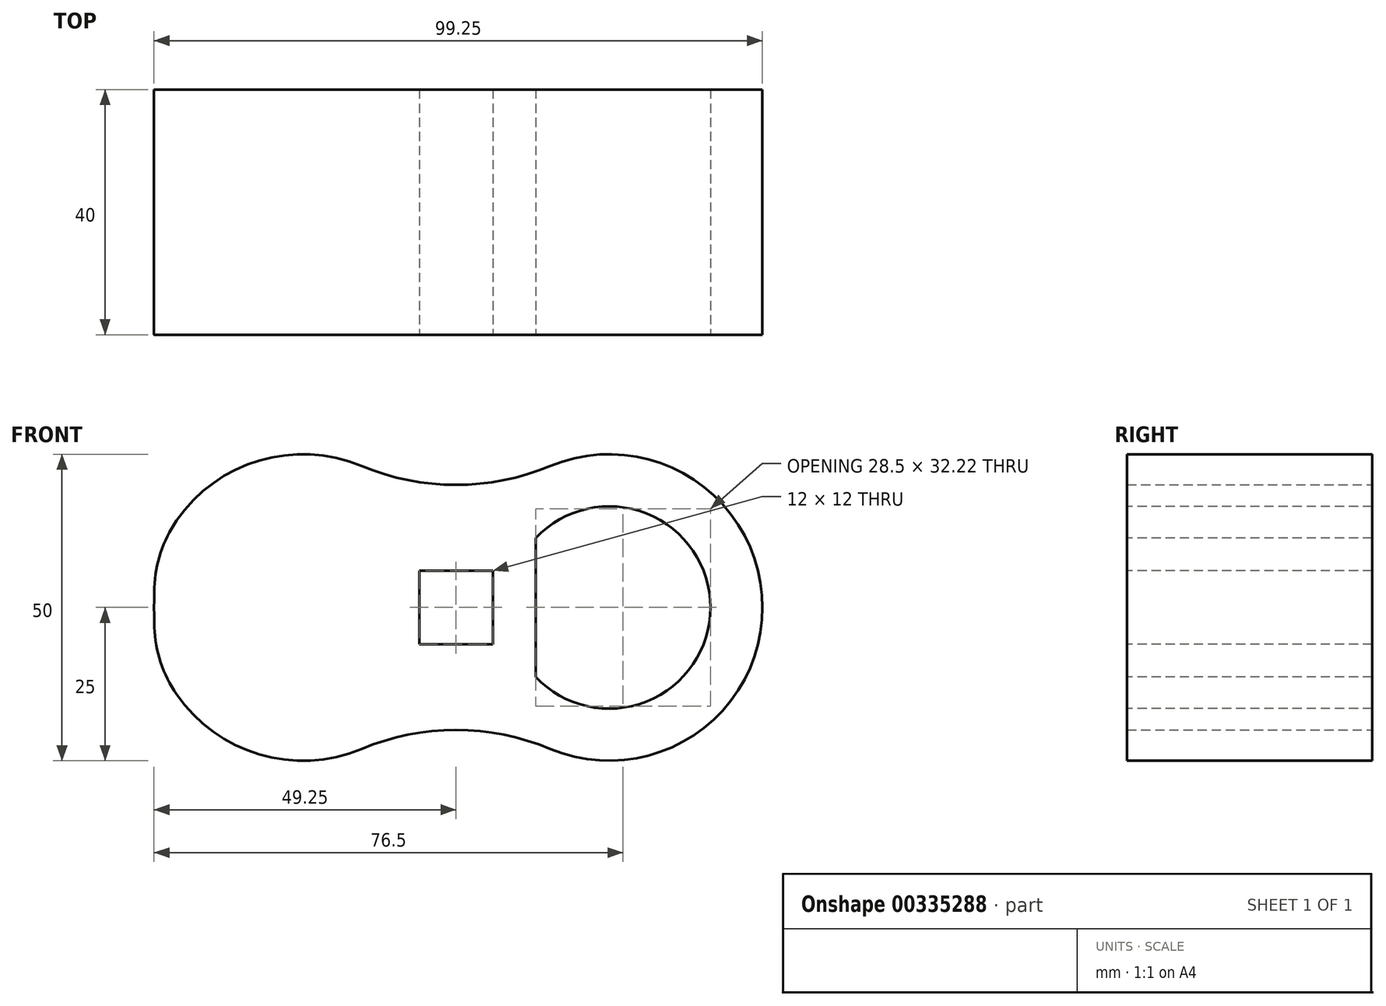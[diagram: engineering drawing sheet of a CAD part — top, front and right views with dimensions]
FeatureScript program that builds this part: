
annotation { "Feature Type Name" : "Feature", "Feature Type Description" : "" }
export const myFeature = defineFeature(function(context is Context, id is Id, definition is map)
    precondition{}
    {
        {
            var Q0;
            Q0=qCreatedBy(makeId("Front.planeOp"),FACE);
            var sketch = newSketch(context, id + "F0", { "sketchPlane" : qUnion([Q0])});
            skCircle(sketch, "E0", {"center": v(-25, 0) * mm, "radius": 25 * mm});
            skCircle(sketch, "E1", {"center": v(25, 0) * mm, "radius": 25 * mm});
            skSolve(sketch);
        }
        {
            var Q0;
            Q0=makeQuery(id+"F0.imprint","IMPRINT",FACE,{"disambiguationData":[TD([[makeQuery(id+"F0.imprint","IMPRINT",EDGE,{"derivedFrom":sQuery(id+"F0.wireOp",EDGE,"E0")}),1.0]])]});
            var Q1;
            Q1=makeQuery(id+"F0.imprint","IMPRINT",FACE,{"disambiguationData":[TD([[makeQuery(id+"F0.imprint","IMPRINT",EDGE,{"derivedFrom":sQuery(id+"F0.wireOp",EDGE,"E1")}),1.0]])]});
            extrude(context, id + "F1", {"entities" : qUnion([Q0, Q1]), "depth" : 40 * mm, "symmetric" : true});
        }
        {
            var Q0;
            Q0=qCreatedBy(makeId("Front.planeOp"),FACE);
            var sketch = newSketch(context, id + "F2", { "sketchPlane" : qUnion([Q0])});
            skCircle(sketch, "E2.0", {"center": v(-25, 0) * mm, "radius": 25 * mm});
            skCircle(sketch, "E3.0", {"center": v(25, 0) * mm, "radius": 25 * mm});
            skArc(sketch, "E4", {"start": v(-15.38, 23.08) * mm, "mid": v(0, 20) * mm, "end": v(15.38, 23.08) * mm});
            skSolve(sketch);
        }
        {
            var Q0;
            {var subQ0=sQuery(id+"F2.wireOp",EDGE,"E4");Q0=makeQuery(id+"F2.imprint","IMPRINT",FACE,{"disambiguationData":[TD([[makeQuery(id+"F2.imprint","IMPRINT",EDGE,{"derivedFrom":subQ0}),-1.0]])]});}
            extrude(context, id + "F3", {"entities" : qUnion([Q0]), "depth" : 40 * mm, "symmetric" : true});
        }
        {
            var Q0;
            Q0=makeQuery(id+"F3.opExtrude","SWEPT_BODY",BODY,{"disambiguationData":[OSD([sQuery(id+"F2.wireOp",EDGE,"E2.0"),sQuery(id+"F2.wireOp",EDGE,"E3.0"),sQuery(id+"F2.wireOp",EDGE,"2BZBx5rq-q8Em-88Co-RqiP-DuQqBopabYor")])]});
            var Q1;
            Q1=qCreatedBy(makeId("Top.planeOp"),FACE);
            mirror(context, id + "F4", {"entities" : qUnion([Q0]), "mirrorPlane" : qUnion([Q1])});
        }
        {
            var Q0;
            Q0=makeQuery(id+"F3.opExtrude","SWEPT_BODY",BODY,{"disambiguationData":[OSD([sQuery(id+"F2.wireOp",EDGE,"E2.0"),sQuery(id+"F2.wireOp",EDGE,"E3.0"),sQuery(id+"F2.wireOp",EDGE,"2BZBx5rq-q8Em-88Co-RqiP-DuQqBopabYor")])]});
            var Q1;
            Q1=makeQuery(id+"F1.opExtrude","SWEPT_BODY",BODY,{"disambiguationData":[OSD([sQuery(id+"F0.wireOp",EDGE,"E1")])]});
            var Q2;
            Q2=makeQuery(id+"F1.opExtrude","SWEPT_BODY",BODY,{"disambiguationData":[OSD([sQuery(id+"F0.wireOp",EDGE,"E0")])]});
            var Q3;
            Q3=makeQuery(id+"F4.opPattern","COPY",BODY,{"derivedFrom":makeQuery(id+"F3.opExtrude","SWEPT_BODY",BODY,{"disambiguationData":[OSD([sQuery(id+"F2.wireOp",EDGE,"E2.0"),sQuery(id+"F2.wireOp",EDGE,"E3.0"),sQuery(id+"F2.wireOp",EDGE,"2BZBx5rq-q8Em-88Co-RqiP-DuQqBopabYor")])]}),"instanceName":"1"});
            booleanBodies(context, id + "F5", {"operationType" : BooleanOperationType.UNION, "tools" : qUnion([Q0, Q1, Q2, Q3])});
        }
        {
            var Q0;
            {var subQ0=makeQuery(id+"F3.opExtrude","CAP_FACE",FACE,{"disambiguationData":[OSD([sQuery(id+"F2.wireOp",EDGE,"E2.0"),sQuery(id+"F2.wireOp",EDGE,"E3.0"),sQuery(id+"F2.wireOp",EDGE,"2BZBx5rq-q8Em-88Co-RqiP-DuQqBopabYor")])],"isStart":false});Q0=makeQuery(id+"F5.opBoolean","MERGE",FACE,{"derivedFrom":[makeQuery(id+"F1.opExtrude","CAP_FACE",FACE,{"disambiguationData":[OSD([sQuery(id+"F0.wireOp",EDGE,"E0")])],"isStart":false}),makeQuery(id+"F1.opExtrude","CAP_FACE",FACE,{"disambiguationData":[OSD([sQuery(id+"F0.wireOp",EDGE,"E1")])],"isStart":false}),subQ0,makeQuery(id+"F4.opPattern","COPY",FACE,{"derivedFrom":subQ0,"instanceName":"1"})]});}
            var sketch = newSketch(context, id + "F6", { "sketchPlane" : qUnion([Q0])});
            skLineSegment(sketch, "E5.bottom", {"start": v(6, 6) * mm, "end": v(-6, 6) * mm});
            skLineSegment(sketch, "E5.top", {"start": v(6, -6) * mm, "end": v(-6, -6) * mm});
            skLineSegment(sketch, "E5.left", {"start": v(6, 6) * mm, "end": v(6, -6) * mm});
            skLineSegment(sketch, "E5.right", {"start": v(-6, 6) * mm, "end": v(-6, -6) * mm});
            skPoint(sketch, "E5.middle", {"position": v(0, 0) * mm});
            skSolve(sketch);
        }
        {
            var Q0;
            Q0=makeQuery(id+"F6.imprint","IMPRINT",FACE,{"disambiguationData":[TD([[makeQuery(id+"F6.imprint","IMPRINT",EDGE,{"derivedFrom":sQuery(id+"F6.wireOp",EDGE,"E5.bottom")}),1.0]])]});
            extrude(context, id + "F7", {"entities" : qUnion([Q0]), "operationType" : NewBodyOperationType.REMOVE, "endBound" : BoundingType.THROUGH_ALL, "oppositeDirection" : true, "depth" : 25 * mm});
        }
        {
            var Q0;
            {var subQ0=makeQuery(id+"F3.opExtrude","CAP_FACE",FACE,{"disambiguationData":[OSD([sQuery(id+"F2.wireOp",EDGE,"E2.0"),sQuery(id+"F2.wireOp",EDGE,"E3.0"),sQuery(id+"F2.wireOp",EDGE,"2BZBx5rq-q8Em-88Co-RqiP-DuQqBopabYor")])],"isStart":false});Q0=makeQuery(id+"F5.opBoolean","MERGE",FACE,{"derivedFrom":[makeQuery(id+"F1.opExtrude","CAP_FACE",FACE,{"disambiguationData":[OSD([sQuery(id+"F0.wireOp",EDGE,"E0")])],"isStart":false}),makeQuery(id+"F1.opExtrude","CAP_FACE",FACE,{"disambiguationData":[OSD([sQuery(id+"F0.wireOp",EDGE,"E1")])],"isStart":false}),subQ0,makeQuery(id+"F4.opPattern","COPY",FACE,{"derivedFrom":subQ0,"instanceName":"1"})]});}
            var sketch = newSketch(context, id + "F8", { "sketchPlane" : qUnion([Q0])});
            skCircle(sketch, "E6", {"center": v(25, 0) * mm, "radius": 16.5 * mm});
            skLineSegment(sketch, "E7", {"start": v(13, 11.32) * mm, "end": v(13, -11.32) * mm});
            skSolve(sketch);
        }
        {
            var Q0;
            {var subQ0=sQuery(id+"F8.wireOp",EDGE,"E7");Q0=makeQuery(id+"F8.imprint","IMPRINT",FACE,{"disambiguationData":[TD([[makeQuery(id+"F8.imprint","IMPRINT",EDGE,{"derivedFrom":subQ0}),1.0]])]});}
            extrude(context, id + "F9", {"entities" : qUnion([Q0]), "operationType" : NewBodyOperationType.REMOVE, "endBound" : BoundingType.THROUGH_ALL, "oppositeDirection" : true, "depth" : 25 * mm});
        }
        {
            var Q0;
            {var subQ0=makeQuery(id+"F3.opExtrude","CAP_FACE",FACE,{"disambiguationData":[OSD([sQuery(id+"F2.wireOp",EDGE,"E2.0"),sQuery(id+"F2.wireOp",EDGE,"E3.0"),sQuery(id+"F2.wireOp",EDGE,"E4")])],"isStart":false});Q0=makeQuery(id+"F5.opBoolean","MERGE",FACE,{"derivedFrom":[makeQuery(id+"F1.opExtrude","CAP_FACE",FACE,{"disambiguationData":[OSD([sQuery(id+"F0.wireOp",EDGE,"E0")])],"isStart":false}),makeQuery(id+"F1.opExtrude","CAP_FACE",FACE,{"disambiguationData":[OSD([sQuery(id+"F0.wireOp",EDGE,"E1")])],"isStart":false}),subQ0,makeQuery(id+"F4.opPattern","COPY",FACE,{"derivedFrom":subQ0,"instanceName":"1"})]});}
            var sketch = newSketch(context, id + "F10", { "sketchPlane" : qUnion([Q0])});
            skArc(sketch, "E8", {"start": v(-48.46, 12.46) * mm, "mid": v(-49.21, -2.8) * mm, "end": v(-47.6, -18) * mm});
            skLineSegment(sketch, "E9", {"start": v(-48.46, 12.46) * mm, "end": v(-58.54, 13.66) * mm});
            skLineSegment(sketch, "E10", {"start": v(-58.54, 13.66) * mm, "end": v(-58.54, -22.82) * mm});
            skLineSegment(sketch, "E11", {"start": v(-58.54, -22.82) * mm, "end": v(-47.6, -18) * mm});
            skSolve(sketch);
        }
        {
            var Q0;
            Q0 = qSketchRegion(id + "F10", true);
            extrude(context, id + "F11", {"entities" : qUnion([Q0]), "operationType" : NewBodyOperationType.REMOVE, "oppositeDirection" : true, "depth" : 40 * mm});
        }
        {
            var Q0;
            Q0=makeQuery(id+"FgXtsFG8VJguosy_3.1.F11.boolean.opBoolean","INTERSECT",EDGE,{"disambiguationData":[OD(0.0)],"derivedFrom":[makeQuery(id+"F1.opExtrude","SWEPT_FACE",FACE,{"disambiguationData":[OSD([sQuery(id+"F0.wireOp",EDGE,"E1")])]}),makeQuery(id+"FgXtsFG8VJguosy_3.1.F11.opExtrude","SWEPT_FACE",FACE,{"disambiguationData":[OSD([sQuery(id+"F10.wireOp",EDGE,"E8")])]})]});
            var Q1;
            Q1=makeQuery(id+"FgXtsFG8VJguosy_3.1.F11.boolean.opBoolean","INTERSECT",EDGE,{"disambiguationData":[OD(1.0)],"derivedFrom":[makeQuery(id+"F1.opExtrude","SWEPT_FACE",FACE,{"disambiguationData":[OSD([sQuery(id+"F0.wireOp",EDGE,"E1")])]}),makeQuery(id+"FgXtsFG8VJguosy_3.1.F11.opExtrude","SWEPT_FACE",FACE,{"disambiguationData":[OSD([sQuery(id+"F10.wireOp",EDGE,"E8")])]})]});
            var Q2;
            Q2=makeQuery(id+"F11.boolean.opBoolean","INTERSECT",EDGE,{"disambiguationData":[OD(0.0)],"derivedFrom":[makeQuery(id+"F1.opExtrude","SWEPT_FACE",FACE,{"disambiguationData":[OSD([sQuery(id+"F0.wireOp",EDGE,"E0")])]}),makeQuery(id+"F11.opExtrude","SWEPT_FACE",FACE,{"disambiguationData":[OSD([sQuery(id+"F10.wireOp",EDGE,"E8")])]})]});
            var Q3;
            Q3=makeQuery(id+"F11.boolean.opBoolean","INTERSECT",EDGE,{"disambiguationData":[OD(1.0)],"derivedFrom":[makeQuery(id+"F1.opExtrude","SWEPT_FACE",FACE,{"disambiguationData":[OSD([sQuery(id+"F0.wireOp",EDGE,"E0")])]}),makeQuery(id+"F11.opExtrude","SWEPT_FACE",FACE,{"disambiguationData":[OSD([sQuery(id+"F10.wireOp",EDGE,"E8")])]})]});
            fillet(context, id + "F12", {"entities" : qUnion([Q0, Q1, Q2, Q3]), "radius" : 20.5 * mm, "tangentPropagation" : true, "allowEdgeOverflow" : false});
        }
    });
